# Revit family: TY-L-TY3311_Metric
name_source: partatom
category: Sprinklers
units: mm (PartAtom-declared; Revit-internal decimal feet)

## family parameters
Always vertical = Yes
Cut with Voids When Loaded = No
Maintain Annotation Orientation = No
OmniClass Number = 23.65.70.17.11.24
OmniClass Title = Fire Fighting Sprinkler Heads
Part Type = Normal
Room Calculation Point = No
Round Connector Dimension = Use Diameter
Shared = No
Work Plane-Based = No

## types (19) — shared parameters
COBie = Yes
COBie.Component.Name = Sprinklers:Sidewall_SIN
COBie.Type = Yes
COBie.Type.AssetType = Fixed
COBie.Type.Category = Pr_70_55_97_84:Sprinklers
COBie.Type.DurationUnit = year
COBie.Type.Manufacturer = Tyco Fire Protection Products
COBie.Type.Material = Brass
COBie.Type.Shape = Cylinder
COBie.Type.Size = 1/2"(DN15)
COBie.Type.WarrantyGuarantorParts = http://tycofsbp.com
Coverage = Standard
K-Factor = 79.9096
Manufacturer = Tyco Fire Protection Products
Manufacturer URL = www.tyco-fire.com
Material_ = Bronze
Model = TY-L
Nominal Diameter 1 = 15 mm
Orifice = Standard
Orifice Size = 0 mm
Outside Diameter 1 = 21 mm
Response = Standard
SIN No = TY3311
Takeout 1 = 64 mm
Technical Data Sheet No = TFP120
zero-valued in all types: COBie.Type.NominalHeight, COBie.Type.NominalLength, COBie.Type.NominalWidth, COBie.Type.ReplacementCost, Default Elevation, Style Id

## per-type parameters (varying)
| type | COBie.Component.Description | COBie.Type.Colour | COBie.Type.Finish | COBie.Type.ModelNumber | COBie.Type.ModelReference | Coverage_ | Description | Finish_ | Part No | Response_ | Temperature Rating |
| Horizontal Sidewall Brass 74°C 5.6K ½" NPT_53-113-1-165 | TY-L Wet Sidewall  137.8°C K80 DN15 NPT Br | Yellow | Natural Brass | 53-113-1-280 | TY-L Wet Sidewall  137.8°C K80 DN15 NPT Br | Standard | TY-L Horizontal Sidewall Wax over Lead 74°C 5.6K ½" NPT | Wax Over Lead | 53-113-8-165 | Standrad | 138 °C |
| Horizontal Sidewall Brass 93°C 5.6K ½" NPT_53-113-1-200 | TY-L Wet Sidewall  93.3°C K80 DN15 NPT Br | Yellow | Natural Brass | 53-113-1-280 | TY-L Wet Sidewall  93.3°C K80 DN15 NPT Br | Standard | TY-L Horizontal Sidewall Brass 93°C 5.6K ½" NPT | Natural Brass | 53-113-1-200 | Standard | 93 °C |
| Horizontal Sidewall Brass 100°C 5.6K ½" NPT_53-113-1-212 | TY-L Wet Sidewall  100°C K80 DN15 NPT Br | Yellow | Natural Brass | 53-113-1-212 | TY-L Wet Sidewall  100°C K80 DN15 NPT Br | Standard | TY-L Horizontal Sidewall Brass 100°C 5.6K ½" NPT | Natural Brass | 53-113-1-212 | Stadnard | 100 °C |
| Horizontal Sidewall Brass 138°C 5.6K ½" NPT_53-113-1-280 | TY-L Wet Sidewall  137.8°C K80 DN15 NPT Br | Yellow | Natural Brass | 53-113-1-280 | TY-L Wet Sidewall  137.8°C K80 DN15 NPT Br | Standard | TY-L Horizontal Sidewall Wax over Lead 74°C 5.6K ½" NPT | Wax Over Lead | 53-113-8-165 | Standrad | 138 °C |
| Horizontal Sidewall Brass 141°C 5.6K ½" NPT_53-113-1-286 | TY-L Wet Sidewall  141.1°C K80 DN15 NPT Br | Yellow | Natural Brass | 53-113-1-280 | TY-L Wet Sidewall  141.1°C K80 DN15 NPT Br | Standard | TY-L Horizontal Sidewall Brass 141°C 5.6K ½" NPT | Natural Brass | 53-113-1-286 | Standrad | 141 °C |
| Horizontal Sidewall Wax 74°C 5.6K ½" NPT_53-113-6-165 | TY-L Wet Sidewall  73.9°C K80 DN15 NPT Wx | Gray | Wax Coated | 53-113-6-165 | TY-L Wet Sidewall  73.9°C K80 DN15 NPT Wx | Standard | TY-L Horizontal Sidewall Wax 74°C 5.6K ½" NPT | Wax Coated | 53-113-6-165 | Standard | 74 °C |
| Horizontal Sidewall Wax 100°C 5.6K ½" NPT_53-113-6-212 | TY-L Wet Sidewall  100°C K80 DN15 NPT Wx | Gray | Wax Coated | 53-113-6-212 | TY-L Wet Sidewall  100°C K80 DN15 NPT Wx | Standard | TY-L Horizontal Sidewall Wax 100°C 5.6K ½" NPT | Wax Coated | 53-113-6-212 | Standard | 100 °C |
| Horizontal Sidewall Lead 74°C 5.6K ½" NPT_53-113-7-165 | TY-L Wet Sidewall  73.9°C K80 DN15 NPT Lead | Gray | Lead Coated | 53-113-7-165 | TY-L Wet Sidewall  73.9°C K80 DN15 NPT Lead | Standard | TY-L Horizontal Sidewall Lead 74°C 5.6K ½" NPT | Lead Coated | 53-113-7-165 | Standard | 74 °C |
| Horizontal Sidewall Lead 93°C 5.6K ½" NPT_53-113-7-200 | TY-L Wet Sidewall  93.3°C K80 DN15 NPT Lead | Gray | Lead Coated | 53-113-7-280 | TY-L Wet Sidewall  93.3°C K80 DN15 NPT Lead | Standard | TY-L Horizontal Sidewall Lead 93°C 5.6K ½" NPT | Lead Coated | 53-113-7-200 | Standard | 93 °C |
| Horizontal Sidewall Lead 100°C 5.6K ½" NPT_53-113-7-212 | TY-L Wet Sidewall  100°C K80 DN15 NPT Lead | Gray | Lead Coated | 53-113-7-212 | TY-L Wet Sidewall  100°C K80 DN15 NPT Lead | Standard | TY-L Horizontal Sidewall Lead 100°C 5.6K ½" NPT | Lead Coated | 53-113-7-212 | Standard | 100 °C |
| Horizontal Sidewall Lead 138°C 5.6K ½" NPT_53-113-7-280 | TY-L Wet Sidewall  137.8°C K80 DN15 NPT Lead | Gray | Lead Coated | 53-113-7-280 | TY-L Wet Sidewall  137.8°C K80 DN15 NPT Lead | Standard | TY-L Horizontal Sidewall Lead 138°C 5.6K ½" NPT | Lead Coated | 53-113-7-280 | Standard | 138 °C |
| Horizontal Sidewall Lead 141°C 5.6K ½" NPT_53-113-7-286 | TY-L Wet Sidewall  141.1°C K80 DN15 NPT Lead | Gray | Lead Coated | 53-113-7-280 | TY-L Wet Sidewall  141.1°C K80 DN15 NPT Lead | Standard | TY-L Horizontal Sidewall Lead 141°C 5.6K ½" NPT | Lead Coated | 53-113-7-286 | Standard | 141 °C |
| Horizontal Sidewall Wax over Lead 74°C 5.6K ½" NPT_53-113-8-165 | TY-L Wet Sidewall  73.9°C K80 DN15 NPT WoL | Gray | Wax Over Lead | 53-113-8-165 | TY-L Wet Sidewall  73.9°C K80 DN15 NPT WoL | Standard | TY-L Horizontal Sidewall Wax over Lead 74°C 5.6K ½" NPT | Wax Over Lead | 53-113-8-165 | Standard | 74 °C |
| Horizontal Sidewall Wax over Lead 100°C 5.6K ½" NPT_53-113-8-212 | TY-L Wet Sidewall  100°C K80 DN15 NPT WoL | Gray | Wax Over Lead | 53-113-8-212 | TY-L Wet Sidewall  100°C K80 DN15 NPT WoL | Standard | TY-L Horizontal Sidewall Wax over Lead 100°C 5.6K ½" NPT | Wax Over Lead | 53-113-8-212 | Standard | 100 °C |
| Horizontal Sidewall Chrome 74°C 5.6K ½" NPT_53-113-9-165 | TY-L Wet Sidewall  73.9°C K80 DN15 NPT Chr | Silver | Chrome Plated | 53-113-9-165 | TY-L Wet Sidewall  73.9°C K80 DN15 NPT Chr | Standrad | TY-L Horizontal Sidewall Chrome 74°C 5.6K ½" NPT | Chrome Plated | 53-113-9-165 | Standard | 74 °C |
| Horizontal Sidewall Chrome 93°C 5.6K ½" NPT_53-113-9-200 | TY-L Wet Sidewall  93.3°C K80 DN15 NPT Chr | Silver | Chrome Plated | 53-113-9-280 | TY-L Wet Sidewall  93.3°C K80 DN15 NPT Chr | Standard | TY-L Horizontal Sidewall Chrome 93°C 5.6K ½" NPT | Chrome Plated | 53-113-9-200 | Standard | 93 °C |
| Horizontal Sidewall Chrome 100°C 5.6K ½" NPT_53-113-9-212 | TY-L Wet Sidewall  100°C K80 DN15 NPT Chr | Silver | Chrome plated | 53-113-9-212 | TY-L Wet Sidewall  100°C K80 DN15 NPT Chr | Standard | TY-L Horizontal Sidewall Chrome 100°C 5.6K ½" NPT | Chrome Plated | 53-113-9-212 | Standard | 100 °C |
| Horizontal Sidewall Chrome 138°C 5.6K ½" NPT_53-113-9-280 | TY-L Wet Sidewall  137.8°C K80 DN15 NPT Chr | Silver | Chrome Plated | 53-113-9-280 | TY-L Wet Sidewall  137.8°C K80 DN15 NPT Chr | Standard | TY-L Horizontal Sidewall Chrome 138°C 5.6K ½" NPT | Chrome Plated | 53-113-9-280 | Standard | 138 °C |
| Horizontal Sidewall Chrome 141°C 5.6K ½" NPT_53-113-9-286 | TY-L Wet Sidewall  141.1°C K80 DN15 NPT Chr | Silver | Chrome plated | 53-113-9-280 | TY-L Wet Sidewall  141.1°C K80 DN15 NPT Chr | Standard | TY-L Horizontal Sidewall Chrome 141°C 5.6K ½" NPT | Chrome Plated | 53-113-9-286 | Standard | 141 °C |

## geometry (parser evidence)
native form markers: Blend x2, Sweep x58
no freeform markers — native parametric forms only
